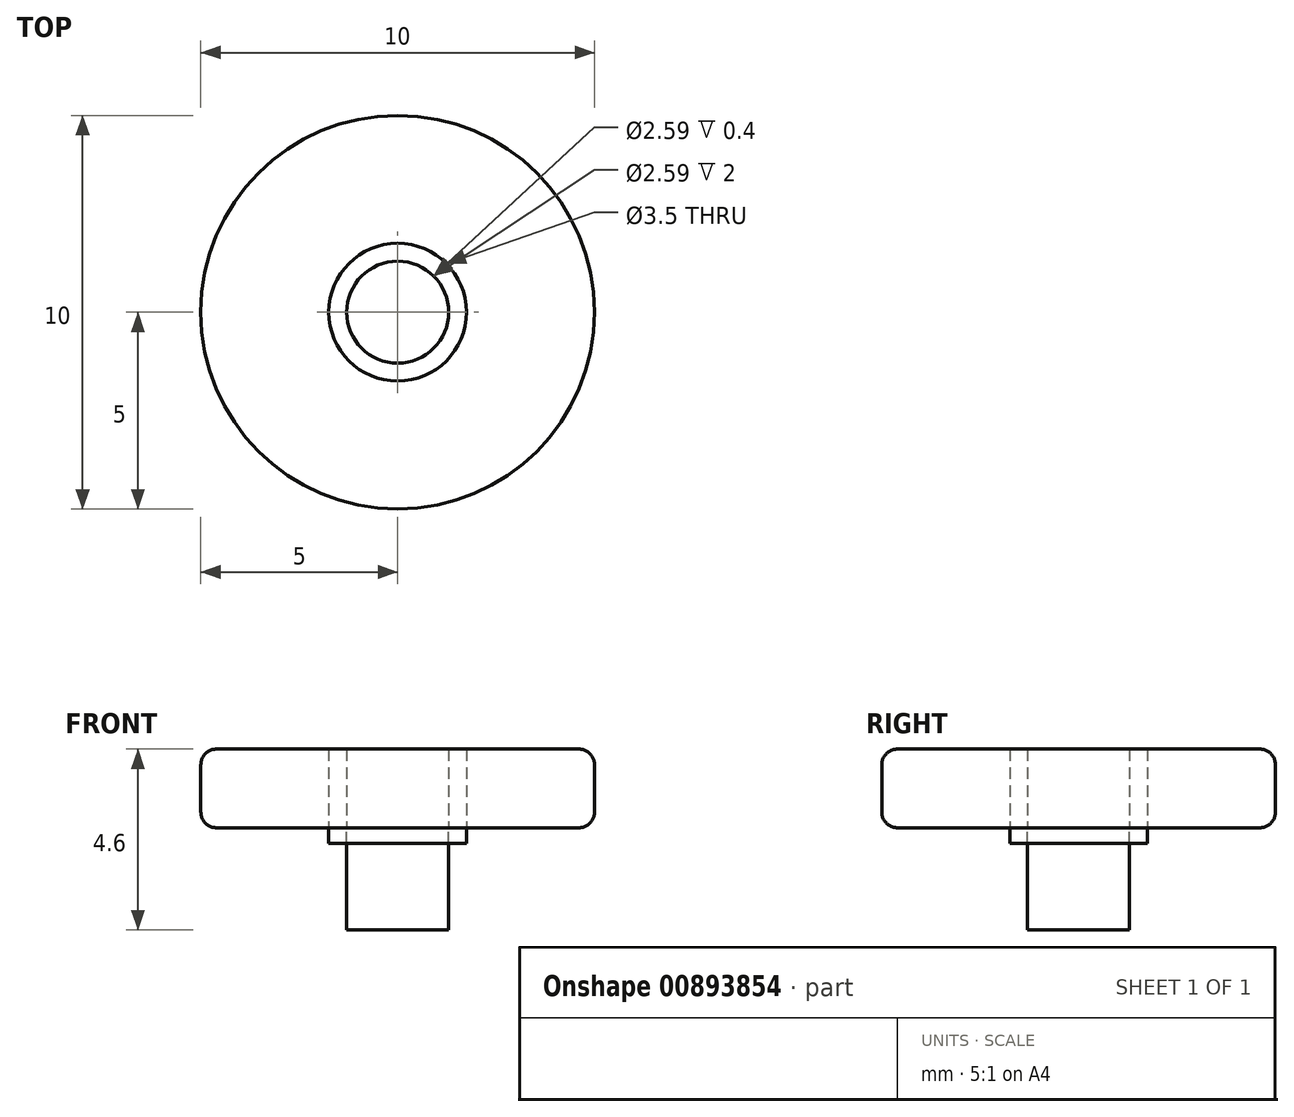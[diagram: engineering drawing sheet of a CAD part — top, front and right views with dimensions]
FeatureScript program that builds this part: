
annotation { "Feature Type Name" : "Feature", "Feature Type Description" : "" }
export const myFeature = defineFeature(function(context is Context, id is Id, definition is map)
    precondition{}
    {
        {
            var Q0;
            Q0=qCreatedBy(makeId("Top.planeOp"),FACE);
            var sketch = newSketch(context, id + "F0", { "sketchPlane" : qUnion([Q0])});
            skCircle(sketch, "E0", {"center": v(0, 0) * mm, "radius": 5 * mm});
            skCircle(sketch, "E1", {"center": v(0, 0) * mm, "radius": 1.3 * mm});
            skCircle(sketch, "E2", {"center": v(0, 0) * mm, "radius": 1.75 * mm});
            skSolve(sketch);
        }
        {
            var Q0;
            Q0 = qSketchRegion(id + "F0", true);
            extrude(context, id + "F1", {"entities" : qUnion([Q0]), "depth" : 2 * mm, "offsetDistance" : 25 * mm});
        }
        {
            var Q0;
            Q0=sQuery(id+"F0.wireOp",EDGE,"E1");
            extrude(context, id + "F2", {"bodyType" : ToolBodyType.SURFACE, "surfaceEntities" : qUnion([Q0]), "oppositeDirection" : true, "depth" : 2.6 * mm, "offsetDistance" : 25 * mm});
        }
        {
            var Q0;
            Q0=makeQuery(id+"F0.imprint","IMPRINT",FACE,{"disambiguationData":[TD([[makeQuery(id+"F0.imprint","IMPRINT",EDGE,{"derivedFrom":sQuery(id+"F0.wireOp",EDGE,"E1")}),1.0]])]});
            extrude(context, id + "F3", {"entities" : qUnion([Q0]), "depth" : 2 * mm, "offsetDistance" : 25 * mm});
        }
        {
            var Q0;
            Q0=makeQuery(id+"F0.imprint","IMPRINT",FACE,{"disambiguationData":[TD([[makeQuery(id+"F0.imprint","IMPRINT",EDGE,{"derivedFrom":sQuery(id+"F0.wireOp",EDGE,"E1")}),-1.0]])]});
            extrude(context, id + "F4", {"entities" : qUnion([Q0]), "oppositeDirection" : true, "depth" : 0.4 * mm, "offsetDistance" : 25 * mm});
        }
        {
            var Q0;
            Q0=makeQuery(id+"F0.imprint","IMPRINT",FACE,{"disambiguationData":[TD([[makeQuery(id+"F0.imprint","IMPRINT",EDGE,{"derivedFrom":sQuery(id+"F0.wireOp",EDGE,"E1")}),-1.0]])]});
            extrude(context, id + "F5", {"entities" : qUnion([Q0]), "depth" : 2 * mm, "offsetDistance" : 25 * mm});
        }
        {
            var Q0;
            Q0=makeQuery(id+"F1.opExtrude","CAP_EDGE",EDGE,{"disambiguationData":[OSD([sQuery(id+"F0.wireOp",EDGE,"E0")])],"isStart":false});
            var Q1;
            Q1=makeQuery(id+"F1.opExtrude","CAP_EDGE",EDGE,{"disambiguationData":[OSD([sQuery(id+"F0.wireOp",EDGE,"E0")])],"isStart":true});
            fillet(context, id + "F6", {"entities" : qUnion([Q0, Q1]), "radius" : 0.4 * mm, "tangentPropagation" : true, "allowEdgeOverflow" : false});
        }
        {
            var Q0;
            Q0=makeQuery(id+"F3.opExtrude","CAP_FACE",FACE,{"disambiguationData":[OSD([sQuery(id+"F0.wireOp",EDGE,"E1")])],"isStart":true});
            extrude(context, id + "F7", {"entities" : qUnion([Q0]), "depth" : 2.6 * mm, "offsetDistance" : 25 * mm});
        }
    });
